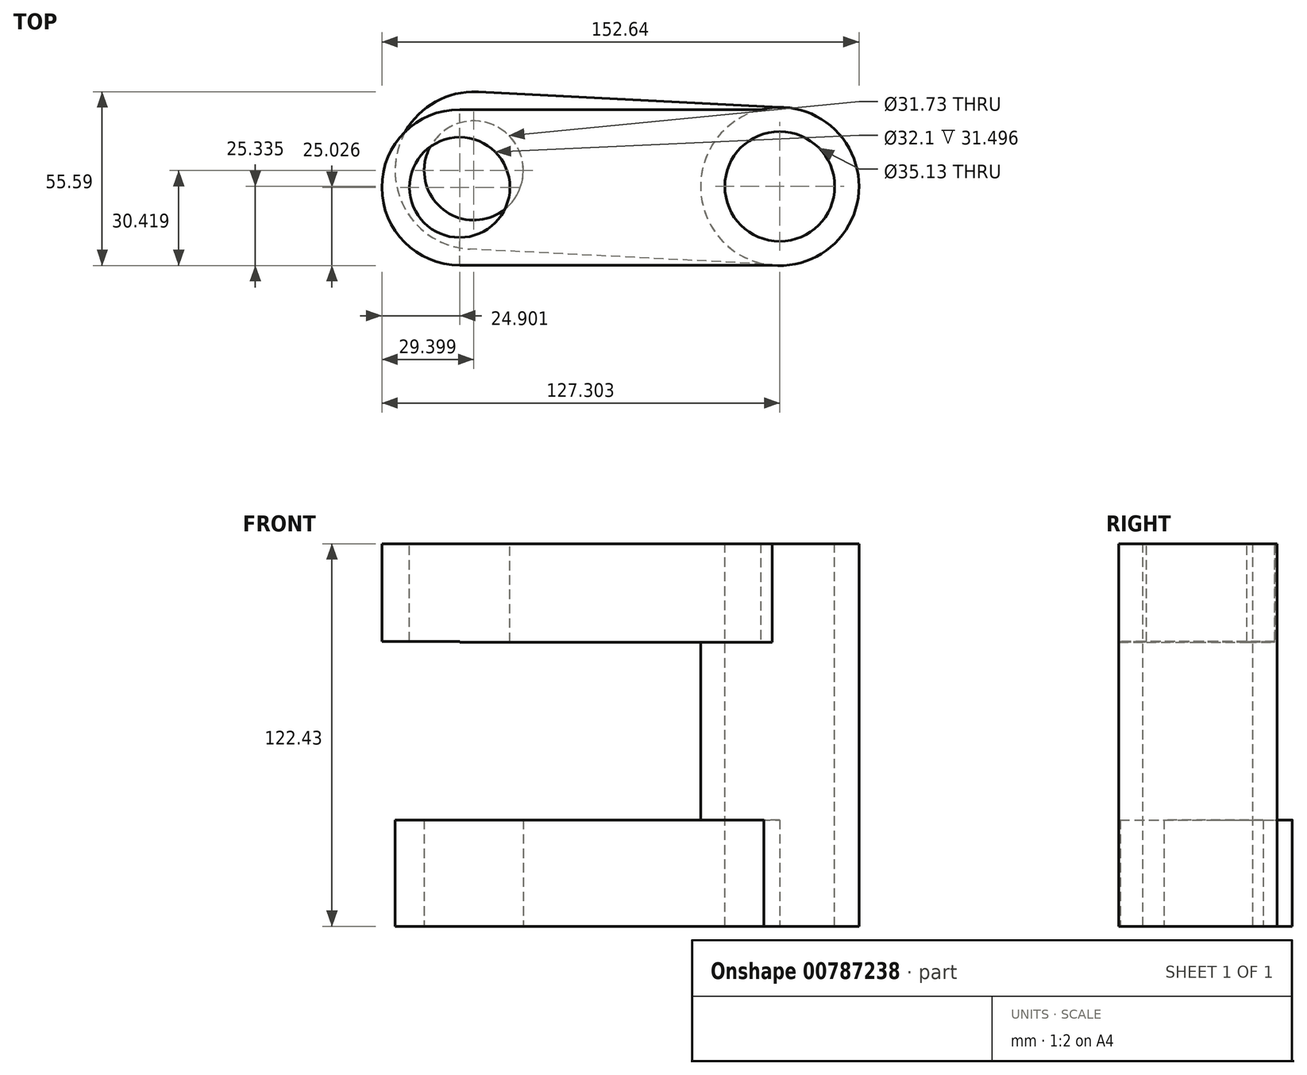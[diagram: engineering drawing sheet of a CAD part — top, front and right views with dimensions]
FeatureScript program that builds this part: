
annotation { "Feature Type Name" : "Feature", "Feature Type Description" : "" }
export const myFeature = defineFeature(function(context is Context, id is Id, definition is map)
    precondition{}
    {
        {
            var Q0;
            Q0=qCreatedBy(makeId("Top.planeOp"),FACE);
            var sketch = newSketch(context, id + "F0", { "sketchPlane" : qUnion([Q0])});
            skCircle(sketch, "E0", {"center": v(21.71, 27.8) * mm, "radius": 25.33 * mm});
            skSolve(sketch);
        }
        {
            var Q0;
            Q0=makeQuery(id+"F0.imprint","IMPRINT",FACE,{"disambiguationData":[TD([[makeQuery(id+"F0.imprint","IMPRINT",EDGE,{"derivedFrom":sQuery(id+"F0.wireOp",EDGE,"E0")}),1.0]])]});
            extrude(context, id + "F1", {"entities" : qUnion([Q0]), "depth" : 122.43 * mm, "offsetDistance" : 25.4 * mm});
        }
        {
            var Q0;
            Q0=makeQuery(id+"F1.opExtrude","CAP_FACE",FACE,{"disambiguationData":[OSD([sQuery(id+"F0.wireOp",EDGE,"E0")])],"isStart":true});
            var sketch = newSketch(context, id + "F2", { "sketchPlane" : qUnion([Q0])});
            skCircle(sketch, "E1", {"center": v(21.71, -27.8) * mm, "radius": 15.22 * mm});
            skLineSegment(sketch, "E2", {"start": v(24.25, -2.59) * mm, "end": v(-77.3, -7.74) * mm});
            skLineSegment(sketch, "E3", {"start": v(24.25, -53) * mm, "end": v(-75.09, -58.02) * mm});
            skLineSegment(sketch, "E4", {"start": v(-75.09, -58.02) * mm, "end": v(-77.3, -7.74) * mm});
            skLineSegment(sketch, "E5", {"start": v(24.25, -53) * mm, "end": v(24.25, -2.59) * mm});
            skSolve(sketch);
        }
        {
            var Q0;
            Q0 = qSketchRegion(id + "F2", true);
            var Q1;
            {var subQ0=sQuery(id+"F2.wireOp",EDGE,"E4");Q1=makeQuery(id+"F2.imprint","IMPRINT",FACE,{"disambiguationData":[TD([[makeQuery(id+"F2.imprint","IMPRINT",EDGE,{"derivedFrom":subQ0}),-1.0]])]});}
            extrude(context, id + "F3", {"entities" : qUnion([Q0, Q1]), "operationType" : NewBodyOperationType.ADD, "oppositeDirection" : true, "depth" : 34.04 * mm, "offsetDistance" : 25.4 * mm});
        }
        {
            var Q0;
            Q0=makeQuery(id+"F3.boolean.opBoolean","MERGE",FACE,{"derivedFrom":[makeQuery(id+"F1.opExtrude","CAP_FACE",FACE,{"disambiguationData":[OSD([sQuery(id+"F0.wireOp",EDGE,"E0")])],"isStart":true}),makeQuery(id+"F3.opExtrude","CAP_FACE",FACE,{"disambiguationData":[OSD([sQuery(id+"F2.wireOp",EDGE,"E1"),sQuery(id+"F2.wireOp",EDGE,"E2"),sQuery(id+"F2.wireOp",EDGE,"E3"),sQuery(id+"F2.wireOp",EDGE,"E4"),sQuery(id+"F2.wireOp",EDGE,"E5")])],"isStart":true})]});
            var sketch = newSketch(context, id + "F4", { "sketchPlane" : qUnion([Q0])});
            skCircle(sketch, "E6", {"center": v(-76.2, -32.88) * mm, "radius": 25.17 * mm});
            skSolve(sketch);
        }
        {
            var Q0;
            Q0 = qSketchRegion(id + "F4", true);
            extrude(context, id + "F5", {"entities" : qUnion([Q0]), "operationType" : NewBodyOperationType.ADD, "oppositeDirection" : true, "depth" : 34.04 * mm, "offsetDistance" : 25.4 * mm});
        }
        {
            var Q0;
            Q0=makeQuery(id+"F1.opExtrude","CAP_FACE",FACE,{"disambiguationData":[OSD([sQuery(id+"F0.wireOp",EDGE,"E0")])],"isStart":false});
            var sketch = newSketch(context, id + "F6", { "sketchPlane" : qUnion([Q0])});
            skLineSegment(sketch, "E7.bottom", {"start": v(19.25, 2.58) * mm, "end": v(-80.69, 2.58) * mm});
            skLineSegment(sketch, "E7.top", {"start": v(19.25, 52.39) * mm, "end": v(-80.69, 52.39) * mm});
            skLineSegment(sketch, "E7.left", {"start": v(19.25, 2.58) * mm, "end": v(19.25, 52.39) * mm});
            skLineSegment(sketch, "E7.right", {"start": v(-80.69, 2.58) * mm, "end": v(-80.69, 52.39) * mm});
            skSolve(sketch);
        }
        {
            var Q0;
            Q0 = qSketchRegion(id + "F6", true);
            extrude(context, id + "F7", {"entities" : qUnion([Q0]), "operationType" : NewBodyOperationType.ADD, "oppositeDirection" : true, "depth" : 31.5 * mm, "offsetDistance" : 25.4 * mm});
        }
        {
            var Q0;
            Q0=makeQuery(id+"F7.boolean.opBoolean","MERGE",FACE,{"derivedFrom":[makeQuery(id+"F1.opExtrude","CAP_FACE",FACE,{"disambiguationData":[OSD([sQuery(id+"F0.wireOp",EDGE,"E0")])],"isStart":false}),makeQuery(id+"F7.opExtrude","CAP_FACE",FACE,{"disambiguationData":[OSD([sQuery(id+"F6.wireOp",EDGE,"E7.bottom"),sQuery(id+"F6.wireOp",EDGE,"E7.top"),sQuery(id+"F6.wireOp",EDGE,"E7.left"),sQuery(id+"F6.wireOp",EDGE,"E7.right")])],"isStart":true})]});
            var sketch = newSketch(context, id + "F8", { "sketchPlane" : qUnion([Q0])});
            skCircle(sketch, "E8", {"center": v(-80.69, 27.49) * mm, "radius": 24.9 * mm});
            skSolve(sketch);
        }
        {
            var Q0;
            {var subQ1=makeQuery(id+"F7.opExtrude","CAP_EDGE",EDGE,{"disambiguationData":[OSD([sQuery(id+"F6.wireOp",EDGE,"E7.right")])],"isStart":true});Q0=makeQuery(id+"F8.imprint","IMPRINT",FACE,{"disambiguationData":[TD([[makeQuery(id+"F8.imprint","IMPRINT",EDGE,{"derivedFrom":subQ1}),1.0]])]});}
            extrude(context, id + "F9", {"entities" : qUnion([Q0]), "operationType" : NewBodyOperationType.ADD, "oppositeDirection" : true, "depth" : 31.24 * mm, "offsetDistance" : 25.4 * mm});
        }
        {
            var Q0;
            {var subQ0=sQuery(id+"F6.wireOp",EDGE,"E7.right");Q0=makeQuery(id+"F9.boolean.opBoolean","MERGE",FACE,{"derivedFrom":[makeQuery(id+"F7.boolean.opBoolean","MERGE",FACE,{"derivedFrom":[makeQuery(id+"F1.opExtrude","CAP_FACE",FACE,{"disambiguationData":[OSD([sQuery(id+"F0.wireOp",EDGE,"E0")])],"isStart":false}),makeQuery(id+"F7.opExtrude","CAP_FACE",FACE,{"disambiguationData":[OSD([sQuery(id+"F6.wireOp",EDGE,"E7.bottom"),sQuery(id+"F6.wireOp",EDGE,"E7.top"),sQuery(id+"F6.wireOp",EDGE,"E7.left"),subQ0])],"isStart":true})]}),makeQuery(id+"F9.opExtrude","CAP_FACE",FACE,{"disambiguationData":[OSD([subQ0,sQuery(id+"F8.wireOp",EDGE,"E8")])],"isStart":true})]});}
            var sketch = newSketch(context, id + "F10", { "sketchPlane" : qUnion([Q0])});
            skCircle(sketch, "E9", {"center": v(-80.69, 27.49) * mm, "radius": 16.05 * mm});
            skCircle(sketch, "E10", {"center": v(21.71, 27.8) * mm, "radius": 16.3 * mm});
            skSolve(sketch);
        }
        {
            var Q0;
            Q0=makeQuery(id+"F5.boolean.opBoolean","MERGE",FACE,{"derivedFrom":[makeQuery(id+"F3.boolean.opBoolean","MERGE",FACE,{"derivedFrom":[makeQuery(id+"F1.opExtrude","CAP_FACE",FACE,{"disambiguationData":[OSD([sQuery(id+"F0.wireOp",EDGE,"E0")])],"isStart":true}),makeQuery(id+"F3.opExtrude","CAP_FACE",FACE,{"disambiguationData":[OSD([sQuery(id+"F2.wireOp",EDGE,"E1"),sQuery(id+"F2.wireOp",EDGE,"E2"),sQuery(id+"F2.wireOp",EDGE,"E3"),sQuery(id+"F2.wireOp",EDGE,"E4"),sQuery(id+"F2.wireOp",EDGE,"E5")])],"isStart":true})]}),makeQuery(id+"F5.opExtrude","CAP_FACE",FACE,{"disambiguationData":[OSD([sQuery(id+"F4.wireOp",EDGE,"E6")])],"isStart":true})]});
            var sketch = newSketch(context, id + "F11", { "sketchPlane" : qUnion([Q0])});
            skCircle(sketch, "E11", {"center": v(-76.2, -32.88) * mm, "radius": 15.87 * mm});
            skSolve(sketch);
        }
        {
            var Q0;
            Q0=makeQuery(id+"F11.imprint","IMPRINT",FACE,{"disambiguationData":[TD([[makeQuery(id+"F11.imprint","IMPRINT",EDGE,{"derivedFrom":sQuery(id+"F11.wireOp",EDGE,"E11")}),1.0]])]});
            extrude(context, id + "F12", {"entities" : qUnion([Q0]), "operationType" : NewBodyOperationType.REMOVE, "oppositeDirection" : true, "depth" : 52.83 * mm, "offsetDistance" : 25.4 * mm});
        }
        {
            var Q0;
            Q0=makeQuery(id+"F10.imprint","IMPRINT",FACE,{"disambiguationData":[TD([[makeQuery(id+"F10.imprint","IMPRINT",EDGE,{"derivedFrom":sQuery(id+"F10.wireOp",EDGE,"E9")}),1.0]])]});
            extrude(context, id + "F13", {"entities" : qUnion([Q0]), "operationType" : NewBodyOperationType.REMOVE, "oppositeDirection" : true, "depth" : 70.1 * mm, "offsetDistance" : 25.4 * mm});
        }
        {
            var Q0;
            {var subQ0=sQuery(id+"F6.wireOp",EDGE,"E7.right");Q0=makeQuery(id+"F9.boolean.opBoolean","MERGE",FACE,{"derivedFrom":[makeQuery(id+"F7.boolean.opBoolean","MERGE",FACE,{"derivedFrom":[makeQuery(id+"F1.opExtrude","CAP_FACE",FACE,{"disambiguationData":[OSD([sQuery(id+"F0.wireOp",EDGE,"E0")])],"isStart":false}),makeQuery(id+"F7.opExtrude","CAP_FACE",FACE,{"disambiguationData":[OSD([sQuery(id+"F6.wireOp",EDGE,"E7.bottom"),sQuery(id+"F6.wireOp",EDGE,"E7.top"),sQuery(id+"F6.wireOp",EDGE,"E7.left"),subQ0])],"isStart":true})]}),makeQuery(id+"F9.opExtrude","CAP_FACE",FACE,{"disambiguationData":[OSD([subQ0,sQuery(id+"F8.wireOp",EDGE,"E8")])],"isStart":true})]});}
            var sketch = newSketch(context, id + "F14", { "sketchPlane" : qUnion([Q0])});
            skCircle(sketch, "E12", {"center": v(21.71, 27.8) * mm, "radius": 17.57 * mm});
            skSolve(sketch);
        }
        {
            var Q0;
            Q0 = qSketchRegion(id + "F14", true);
            extrude(context, id + "F15", {"entities" : qUnion([Q0]), "operationType" : NewBodyOperationType.REMOVE, "oppositeDirection" : true, "depth" : 262.38 * mm, "offsetDistance" : 25.4 * mm});
        }
    });
